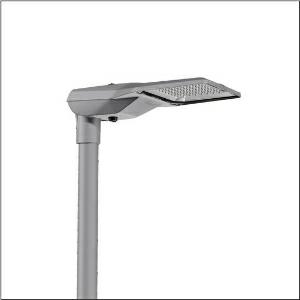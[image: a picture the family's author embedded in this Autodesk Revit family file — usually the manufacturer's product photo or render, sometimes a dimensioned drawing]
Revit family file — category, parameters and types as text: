
# Revit family: streetlight_sl_21_iq_midi___p1_0a_5xe3a31y08mb_7489
name_source: partatom
category: Lighting Fixtures
units: mm (PartAtom-declared; Revit-internal decimal feet)

## family parameters
Cut with Voids When Loaded = No
Host = Face
Light Source = No
Part Type = Normal
Room Calculation Point = No
Round Connector Dimension = Use Diameter
Shared = No

## types (1)
- --- (1 x LED, 18340 lm, 129.3 W, 3000K)
    Apparent Load = 129 VA
    CIE Flux Codes = 21 50 90 100 100
    Color Rendering = 70
    Color Temperature = 3000K
    Default Elevation = 1800 mm
    Description = Streetlight SL 21 iQ midi, mast luminaire, primary light control with lens, of PMMA, primary optical cover: cover, of toughened safety glass, transparent, light distribution: P1.0a, light emission: direct distribution, primary light characteristic: asymmetric, installation type: post-top, side-entry, LED, High Power LED, rated luminous flux: 18.340lm, luminous efficacy: 142lm/W, light colour: 730, colour temperature: 3000K, control gear: iQ-Street Remote, D4i with power reduction, control: pre-setting: logarithmic dimming characteristic, Street-Remote, Auto-Match, Temp-Guard, Lumen-Switch, Night-Set, Smart-Wire, Light-Fading, Desk-Remote (wireless, voltage-free reading and setting of iQ features in the workshop via application-optimized NFC function/RFID function), optimised constant luminous flux control (CLO 2.0), mains connection: 230..240V, AC, 50/60Hz, start of lifetime: 129W, end of service life: 142W, reduction: 56W, luminaire housing, of diecast aluminium, powder-coated, Siteco® metallic grey (DB 702S), corrosivity category C5 mid according to DIN EN ISO 12944, please order mast flange separately, inclination adjustable: 0°, 5°, 10°, 15°, sealing non-destructively replaceable, multi-level sealing system, length: 644mm, width: 335mm, height: 110mm, mast flange for spigot size: 42mm (side-entry): 5XC10008XM4, 60/48mm (side-entry/post-top): 5XC10108XM2, 76/60mm (side-entry/post-top): 5XC10108XM1, mounting height: 4..8m, Smart Interface below and above, protection rating (complete): IP66, insulation class (complete): insulation class II (safety insulation), certification: CE, ENEC, ENEC+, VDE, impact resistance: IK10, permissible operating ambient temperature for outdoor applications: -40..+50°C, standard-compliant lighting for roads and squares, packaging unit: 1 piece

Light Distribution: P1.0a
    Height = 111 mm
    Lamp = 1 x LED
    Lamp Light Flux = 18340 lm
    Lamp Power = 129.3 W
    Lamp count = 1
    Length = 644 mm
    Luminous efficacy = 142 lm/W
    Manufacturer = Siteco
    ModVariant = No
    Model = 5XE3A31Y08MB
    Number of Poles = 1
    OnlyDefault = Yes
    Power Factor = 1
    Product Name = Streetlight SL 21 iQ midi | P1.0a
    Product group = mast luminaire | pylon top
    ProductGroupID = 6100
    Protection Class = Protection class II
    Protection Degree = IP 66
    RLX_Detail_Level = 1
    RLX_Emergency_Light_Flux = 0 lm
    RLX_Emergency_Type = 0
    RLX_Emergency_Type_DB = No
    RlxData = <blob elided: 38421 chars, md5=81753a87>
    Socket = socket
    Standby Power = 0 W
    System Light Flux = 18340 lm
    System Power = 129 W
    Type Comments = factory setting: luminous flux: 100 % | dim-lin: 254 | 672 mA
    Type Image = l_1004304.jpg
    URL = http://relux.com
    VarID = @adj_113462
    Voltage = 0 V
    Weight = 0.00 kg
    Width = 336 mm

## geometry (parser evidence)
native form markers: Blend x4, Sweep x11
no freeform markers — native parametric forms only
